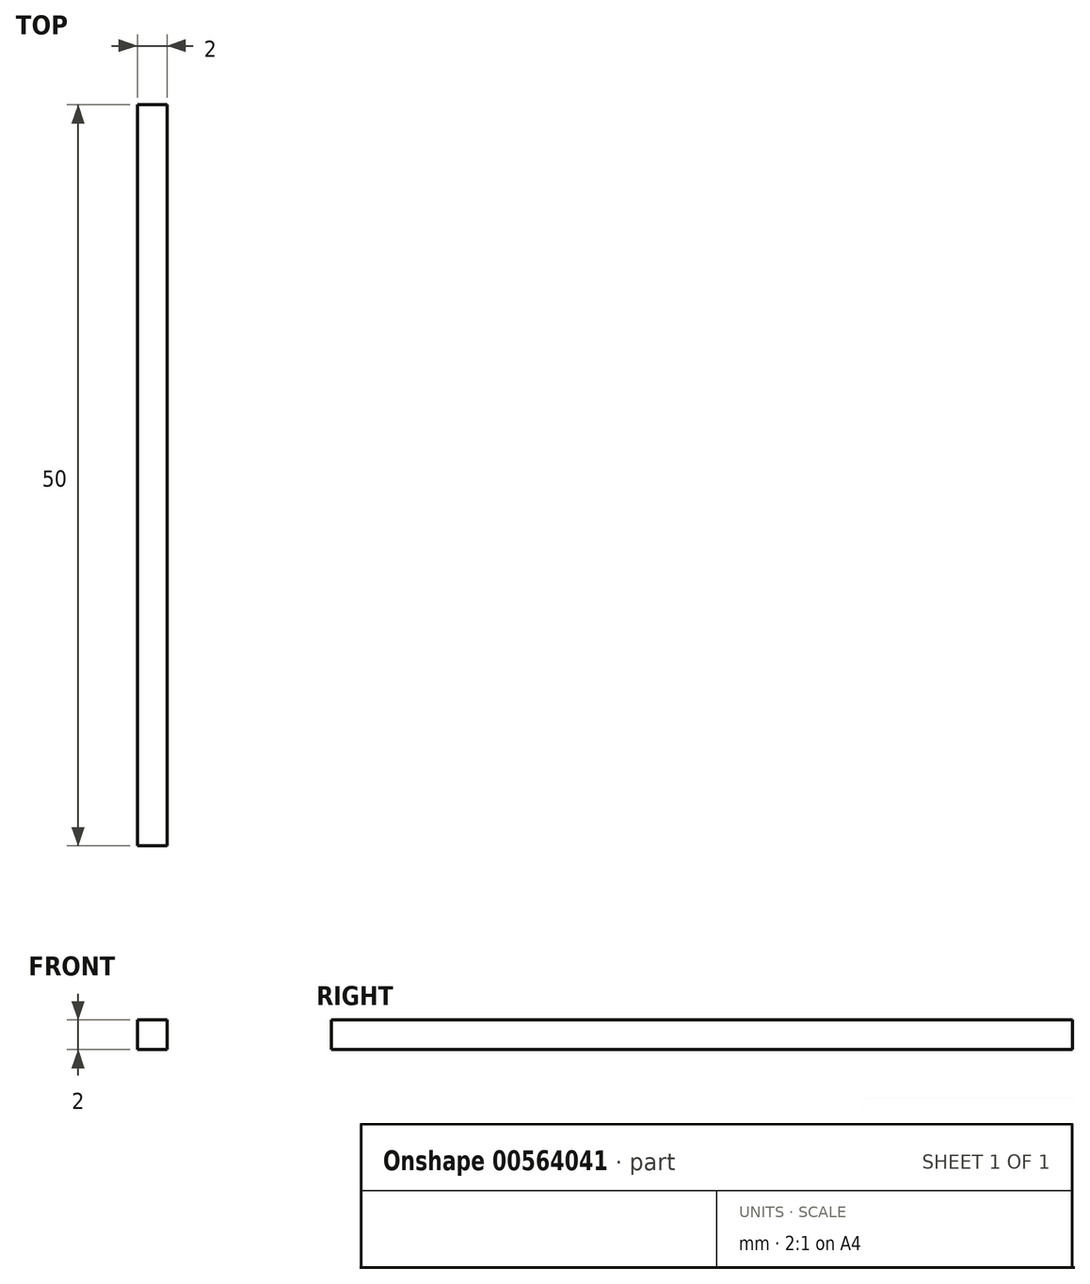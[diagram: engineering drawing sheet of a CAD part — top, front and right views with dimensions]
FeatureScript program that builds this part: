
annotation { "Feature Type Name" : "Feature", "Feature Type Description" : "" }
export const myFeature = defineFeature(function(context is Context, id is Id, definition is map)
    precondition{}
    {
        {
            var Q0;
            Q0=qCreatedBy(makeId("Front.planeOp"), FACE);
            var sketch = newSketch(context, id + "F0", { "sketchPlane" : qUnion([Q0])});
            skLineSegment(sketch, "E0.bottom", {"start": v(-4.66, 0) * mm, "end": v(-6.66, 0) * mm});
            skLineSegment(sketch, "E0.top", {"start": v(-4.66, 2) * mm, "end": v(-6.66, 2) * mm});
            skLineSegment(sketch, "E0.left", {"start": v(-4.66, 0) * mm, "end": v(-4.66, 2) * mm});
            skLineSegment(sketch, "E0.right", {"start": v(-6.66, 0) * mm, "end": v(-6.66, 2) * mm});
            skSolve(sketch);
        }
        {
            var Q0;
            Q0 = qSketchRegion(id + "F0", true);
            extrude(context, id + "F1", {"entities" : qUnion([Q0]), "depth" : 50 * mm, "offsetDistance" : 25 * mm});
        }
    });
